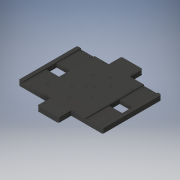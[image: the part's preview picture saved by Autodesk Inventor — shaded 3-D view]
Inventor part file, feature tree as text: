
AUTODESK INVENTOR PART (.ipt)
format: ipt  version: 2017 (Build 210142000, 142)  size: 415,232 bytes
history: native  units: in
note: dims shown in document units (in); Inventor stores cm internally (conversion verified against a paired STEP export)
features: extrude x10, sketch x10, projected_geometry x10, fillet x1
ambient origin geometry x8: Origin, YZ Plane, XZ Plane, XY Plane, X Axis, Y Axis, Z Axis, Center Point
bodies: Solid1 (feature_tree)
feature tree (31):
  extrude  "Extrusion1"  Depth=9.0in
  extrude  "Extrusion2"  Depth=1.118in
  extrude  "Extrusion3"  Depth=0.5in
  extrude  "Extrusion4"  TaperAngle=0.0deg  [1 undecoded]
  extrude  "Extrusion5"  Depth=0.375in
  extrude  "Extrusion7"  Depth=0.125in
  extrude  "ardMount"  Depth=0.125in TaperAngle=0.0deg
  extrude  "piMount"  Depth=0.125in TaperAngle=0.0deg
  extrude  "sabertoothMount"  Depth=3.0in
  extrude  "Extrusion11"  Depth=0.125in TaperAngle=0.0deg
  fillet  "Fillet1"  Radius=1.368in
  sketch  "Sketch1"  dims[d0=9.0in d1=9.0in]
  sketch  "Sketch2"  dims[d2=2.3622in d3=1.118in]
  projected_geometry  "Projected Loop1"
  sketch  "Sketch3"  dims[d4=0.5in d5=0.0in d6=0.25in]
  projected_geometry  "Projected Loop2"
  projected_geometry  "Projected Loop3"
  projected_geometry  "Projected Loop4"
  projected_geometry  "Projected Loop5"
  sketch  "Sketch4"  dims[d7=0.375in d8=0.0in]
  sketch  "Sketch5"  dims[d9=1.5in d10=0.375in]
  sketch  "Sketch7"  dims[d11=0.125in d12=0.5827in]
  projected_geometry  "Projected Loop7"
  sketch  "Sketch8"  dims[d13=0.125in d14=0.0312in d15=0.0in]
  projected_geometry  "Projected Loop8"
  sketch  "Sketch9"  dims[d16=0.125in d17=0.0in d18=0.125in d19=0.0in]
  projected_geometry  "Projected Loop9"
  sketch  "Sketch10"  dims[d20=1.5in d21=3.0in]
  projected_geometry  "Projected Loop10"
  sketch  "Sketch11"  dims[d22=0.125in d23=0.125in d24=0.0in d30=1.368in d31=1.0in d32=0.0in d33=0.172in d34=3.543in d35=0.63in d36=0.172in d37=0.571in d38=3.799in d39=0.125in d40=0.125in d41=0.125in d42=0.125in d43=1.0in d44=0.0in d45=0.161in d46=0.93in d47=3.21in d48=0.125in d49=0.125in d50=1.0in d51=0.0in d52=2.026in d53=2.86in d54=1.12in d55=4.275in d56=2.026in d57=2.86in d58=1.12in d59=4.275in d60=0.125in d61=0.125in d62=0.125in d63=0.125in d64=0.125in d65=0.125in d66=0.125in d67=0.125in d68=1.0in d69=0.0in d70=1.125in d71=1.0in d72=0.0in d73=0.125in d74=0.172in]
  projected_geometry  "Projected Loop11"
note: 1 required parameter value undecoded (feature->parameter linkage not recoverable at this tier; creation-order binding heuristic only, values carry confidence <= 0.55)
